# Revit family: Haworth_Maari_Chair_LegBase_EU_PRELIMINARY
name_source: partatom
category: Furniture
units: mm (PartAtom-declared; Revit-internal decimal feet)

## family parameters
Always vertical = Yes
Cut with Voids When Loaded = No
OmniClass Number = 23.40.70.14.64.21
OmniClass Title = Systems Furniture
Room Calculation Point = No
Shared = No
Work Plane-Based = No

## types (5) — shared parameters
Actual Depth = 55 cm
Arm Cap Finish = Haworth _ Polymer _ Undecided
Assembly Code = E2020200
Glide or Caster Option = Option only available for Four-Leg Chair
Manufacturer = Haworth
Model = SEMIGX
Revision Number = 2
Size = Verify Final Dim. w/ Haworth
URL = https://www.haworth.com
URL - Product = https://www.haworth.com
Warranty = http://www.haworth.com

## per-type parameters (varying)
| type | Actual Height | Actual Width | Casters | Description | Four Leg Arm Control | Four Legs | Glides | Sled Base | Sled Leg Arm Control | With Arms | Wood Base |
| Wood Legs - No Arms | 86 cm | 50 cm | No | Haworth - Maari - Chair - Wood Legs | No | No | Yes | No | No | No | Yes |
| Sled Base - With Arms | 86 cm | 56 cm | No | Haworth - Maari - Chair - Sled Base | No | No | Yes | Yes | Yes | Yes | No |
| Four Leg - With Arms | 84 cm | 58 cm | Yes | Haworth - Maari - Chair - Four Leg | Yes | Yes | No | No | No | Yes | No |
| Four Leg - No Arms | 84 cm | 58 cm | Yes | Haworth - Maari - Chair - Four Leg | No | Yes | No | No | No | No | No |
| Sled Base - No Arms | 86 cm | 56 cm | No | Haworth - Maari - Chair - Sled Base | No | No | Yes | Yes | No | No | No |

## geometry (parser evidence)
native form markers: Sweep x9
no freeform markers — native parametric forms only
